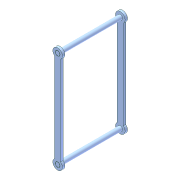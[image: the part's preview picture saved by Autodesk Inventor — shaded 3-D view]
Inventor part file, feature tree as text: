
AUTODESK INVENTOR PART (.ipt)
format: ipt  version: unknown  size: 192,512 bytes
history: native  units: in
note: dims shown in document units (in); Inventor stores cm internally (conversion verified against a paired STEP export)
features: extrude x2, sketch x2, plane x1, mirror x1
ambient origin geometry x8: Origin, YZ Plane, XZ Plane, XY Plane, X Axis, Y Axis, Z Axis, Center Point
feature tree (6):
  extrude  "Extrusion43"  Depth=0.1575in
  plane  "Work Plane1"
  mirror  "Mirror3"
  extrude  "Extrusion44"  Depth=0.0984in
  sketch  "Sketch43"  dims[d200=0.0787in d201=0.1575in]
  sketch  "Sketch44"  dims[d202=0.0492in d203=0.0984in d204=1.5748in d205=0.0394in d206=0.0in d207=0.4921in d208=0.0709in d209=0.0709in d210=1.063in d211=0.0in]
